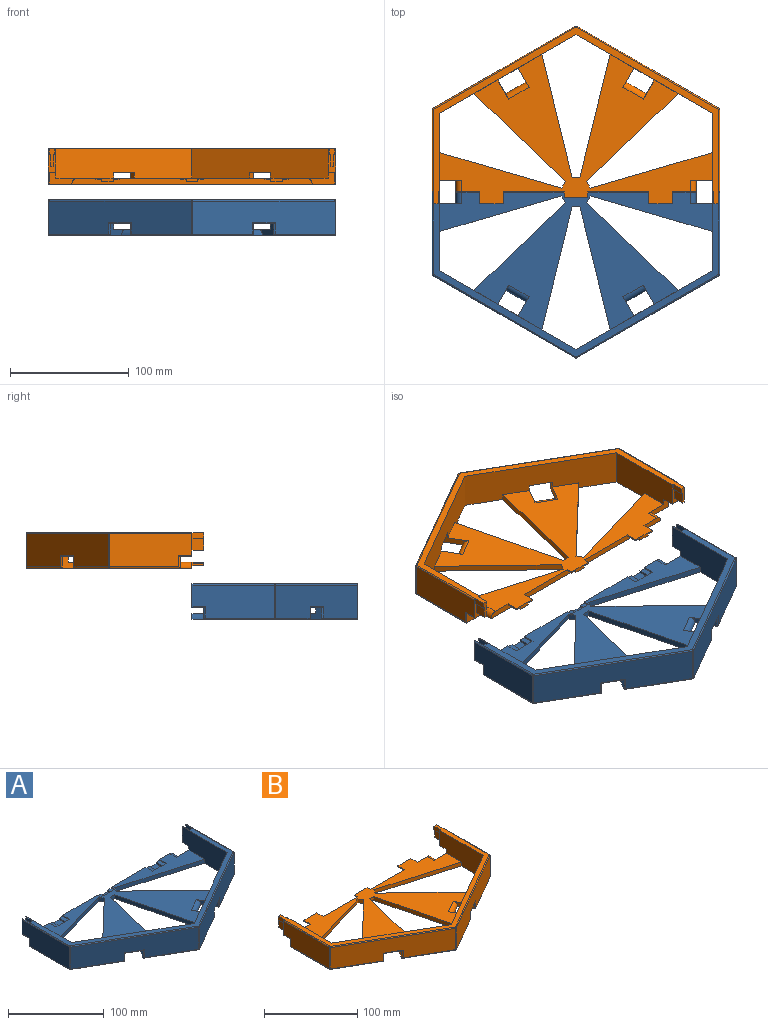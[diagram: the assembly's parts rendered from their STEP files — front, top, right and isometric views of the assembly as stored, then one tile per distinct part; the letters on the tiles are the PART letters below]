
ASSEMBLY  parts=2 mates=1
PART A: 106 faces, bbox 242.5x139.8x30 mm
  f0: plane 229.5x115.94mm, normal (0,0,1), area 9823.1mm2, adj f1,f3,f6,f8,f13,f14,f15,f16
  f1: plane 202.49x5mm, normal (0,1,0), area 870.5mm2, adj f0,f4,f49,f50,f51,f52,f53,f54
  f2: plane 240.49x138.85mm, normal (0,0,1), area 2146.7mm2, adj f3,f5,f6,f8,f9,f13,f39,f40
  f3: plane 114.75x66.25mm, normal (0.5,0.87,0), area 3543.8mm2, adj f0,f2,f4,f6,f8,f15,f20,f30
  f4: plane 240.49x138.85mm, normal (0,0,-1), area 12530mm2, adj f1,f3,f6,f8,f13,f14,f15,f16
  f5: plane 20x6.5mm, normal (0,1,0), area 82mm2, adj f2,f6,f10,f28,f41,f42,f43,f44
  f6: plane 66.25x30mm, normal (1,0,0), area 1771.9mm2, adj f0,f2,f3,f4,f5,f14,f28,f29
  f7: plane 69.42x28mm, normal (1,0,0), area 1833.8mm2, adj f9,f73,f74,f76,f82,f83
  f8: plane 114.75x66.25mm, normal (-0.5,0.87,0), area 3543.8mm2, adj f0,f2,f3,f4,f13,f18,f21,f23
  f9: plane 20x6.5mm, normal (0,1,0), area 82mm2, adj f2,f7,f13,f26,f33,f34,f35,f36
  f10: plane 69.42x28mm, normal (-1,0,0), area 1833.8mm2, adj f5,f75,f77,f79,f80,f81
  f11: plane 120.24x69.42mm, normal (-0.5,-0.87,0), area 3667.7mm2, adj f80,f89,f90,f93,f96,f97,f99,f101
  f12: plane 120.24x69.42mm, normal (0.5,-0.87,0), area 3667.7mm2, adj f83,f84,f88,f91,f92,f95,f97,f98
  f13: plane 66.25x30mm, normal (-1,0,0), area 1771.9mm2, adj f0,f2,f4,f8,f9,f17,f26,f27
  f14: plane 102.67x29.89mm, normal (0.28,-0.96,0), area 534.7mm2, adj f0,f4,f6,f16
  f15: plane 77.22x73.97mm, normal (-0.69,0.72,0), area 534.7mm2, adj f0,f3,f4,f16
  f16: plane 5.6x5mm, normal (-0.87,-0.5,0), area 32.4mm2, adj f0,f4,f14,f15
  f17: plane 102.67x29.89mm, normal (-0.28,-0.96,0), area 534.7mm2, adj f0,f4,f13,f19
  f18: plane 77.22x73.98mm, normal (0.69,0.72,0), area 534.7mm2, adj f0,f4,f8,f19
  f19: plane 5.6x5mm, normal (0.87,-0.5,0), area 32.4mm2, adj f0,f4,f17,f18
  f20: plane 103.86x25.46mm, normal (0.97,-0.24,0), area 534.7mm2, adj f0,f3,f4,f22
  f21: plane 103.86x25.46mm, normal (-0.97,-0.24,0), area 534.7mm2, adj f0,f4,f8,f22
  f22: plane 6.47x5mm, normal (0,-1,0), area 32.4mm2, adj f0,f4,f20,f21
  f23: plane 20.07x14.76mm, normal (0,0,-1), area 109.9mm2, adj f8,f24,f25,f92
  f24: plane 20.78x12mm, normal (0.87,0.5,0), area 127.8mm2, adj f0,f4,f8,f23,f95,f105
  f25: plane 20.78x12mm, normal (-0.87,-0.5,0), area 127.8mm2, adj f0,f4,f8,f23,f88,f105
  f26: plane 10x5.5mm, normal (0,0,-1), area 55mm2, adj f9,f13,f27,f73
  f27: plane 24x10mm, normal (0,1,0), area 127.8mm2, adj f0,f4,f13,f26,f74,f104
  f28: plane 10x5.5mm, normal (0,0,-1), area 55mm2, adj f5,f6,f29,f75
  f29: plane 24x10mm, normal (0,1,0), area 127.8mm2, adj f0,f4,f6,f28,f77,f103
  f30: plane 20.07x14.76mm, normal (0,0,-1), area 109.9mm2, adj f3,f31,f32,f96
  f31: plane 20.78x12mm, normal (0.87,-0.5,0), area 127.8mm2, adj f0,f3,f4,f30,f93,f102
  f32: plane 20.78x12mm, normal (-0.87,0.5,0), area 127.8mm2, adj f0,f3,f4,f30,f99,f102
  f33: plane 10x5mm, normal (-1,0,0), area 50mm2, adj f9,f34,f40,f82
  f34: plane 10x1mm, normal (0,0,1), area 10mm2, adj f9,f33,f35,f40
  f35: plane 10x10mm, normal (-1,0,0), area 100mm2, adj f9,f34,f36,f40
  f36: plane 10x2.5mm, normal (0,0,1), area 25mm2, adj f9,f35,f37,f40
  f37: plane 10x10mm, normal (1,0,0), area 100mm2, adj f9,f36,f38,f40
  f38: plane 10x1mm, normal (0,0,1), area 10mm2, adj f9,f37,f39,f40
  f39: plane 10x5mm, normal (1,0,0), area 50mm2, adj f2,f9,f38,f40
  f40: plane 15x4.5mm, normal (0,1,0), area 47.4mm2, adj f2,f33,f34,f35,f36,f37,f38,f39
  f41: plane 10x5mm, normal (-1,0,0), area 50mm2, adj f2,f5,f42,f48
  f42: plane 10x1mm, normal (0,0,1), area 10mm2, adj f5,f41,f43,f48
  f43: plane 10x10mm, normal (-1,0,0), area 100mm2, adj f5,f42,f44,f48
  f44: plane 10x2.5mm, normal (0,0,1), area 25mm2, adj f5,f43,f45,f48
  f45: plane 10x10mm, normal (1,0,0), area 100mm2, adj f5,f44,f46,f48
  f46: plane 10x1mm, normal (0,0,1), area 10mm2, adj f5,f45,f47,f48
  f47: plane 10x5mm, normal (1,0,0), area 50mm2, adj f5,f46,f48,f81
  f48: plane 15x4.5mm, normal (0,1,0), area 47.4mm2, adj f2,f41,f42,f43,f44,f45,f46,f47
  f49: plane 10x5mm, normal (0,0,1), area 50mm2, adj f1,f50,f55,f56
  f50: plane 10x1.25mm, normal (1,0,0), area 12.5mm2, adj f0,f1,f49,f56
  f51: plane 10x1.25mm, normal (-1,0,0), area 12.5mm2, adj f0,f1,f52,f56
  f52: plane 10x5mm, normal (0,0,1), area 50mm2, adj f1,f51,f53,f56
  f53: plane 10x1.88mm, normal (-1,0,0), area 18.8mm2, adj f1,f52,f54,f56
  f54: plane 10x10mm, normal (0,0,1), area 100mm2, adj f1,f53,f55,f56
  f55: plane 10x1.88mm, normal (1,0,0), area 18.8mm2, adj f1,f49,f54,f56
  f56: plane 20x3.13mm, normal (0,1,0), area 43.8mm2, adj f0,f49,f50,f51,f52,f53,f54,f55
  f57: plane 10x1.25mm, normal (-1,0,0), area 12.5mm2, adj f0,f1,f58,f64
  f58: plane 10x5mm, normal (0,0,1), area 50mm2, adj f1,f57,f59,f64
  f59: plane 10x1.88mm, normal (-1,0,0), area 18.8mm2, adj f1,f58,f60,f64
  f60: plane 10x10mm, normal (0,0,1), area 100mm2, adj f1,f59,f61,f64
  f61: plane 10x1.88mm, normal (1,0,0), area 18.8mm2, adj f1,f60,f62,f64
  f62: plane 10x5mm, normal (0,0,1), area 50mm2, adj f1,f61,f63,f64
  f63: plane 10x1.25mm, normal (1,0,0), area 12.5mm2, adj f0,f1,f62,f64
  f64: plane 20x3.13mm, normal (0,1,0), area 43.8mm2, adj f0,f57,f58,f59,f60,f61,f62,f63
  f65: plane 10x5mm, normal (0,0,1), area 50mm2, adj f1,f66,f71,f72
  f66: plane 5x1.88mm, normal (1,0,0), area 9.4mm2, adj f1,f65,f67,f72
  f67: plane 5x5mm, normal (0,0,1), area 25mm2, adj f1,f66,f68,f72
  f68: plane 5x1.25mm, normal (1,0,0), area 6.3mm2, adj f0,f1,f67,f72
  f69: plane 5x1.25mm, normal (-1,0,0), area 6.3mm2, adj f0,f1,f70,f72
  f70: plane 5x5mm, normal (0,0,1), area 25mm2, adj f1,f69,f71,f72
  f71: plane 5x1.88mm, normal (-1,0,0), area 9.4mm2, adj f1,f65,f70,f72
  f72: plane 20x3.13mm, normal (0,1,0), area 43.8mm2, adj f0,f65,f66,f67,f68,f69,f70,f71
  f73: cylinder r=1mm len=11mm, axis (0,-1,0), area 16.3mm2, adj f7,f9,f26,f74
  f74: cylinder r=1mm len=11mm, axis (0,0,-1), area 15.7mm2, adj f7,f27,f73,f76
  f75: cylinder r=1mm len=11mm, axis (0,1,0), area 16.3mm2, adj f5,f10,f28,f77
  f76: cylinder r=1mm len=59.42mm, axis (0,1,0), area 92.8mm2, adj f4,f7,f74,f78
  f77: cylinder r=1mm len=11mm, axis (0,0,1), area 15.7mm2, adj f10,f29,f75,f79
  f78: sphere r=1mm, area 1mm2, adj f76,f83,f84
  f79: cylinder r=1mm len=59.42mm, axis (0,-1,0), area 92.8mm2, adj f4,f10,f77,f85
  f80: cylinder r=1mm len=28mm, axis (0,0,-1), area 29.3mm2, adj f10,f11,f85,f86
  f81: cylinder r=1mm len=69.42mm, axis (0,1,0), area 109mm2, adj f2,f5,f10,f47,f86
  f82: cylinder r=1mm len=69.42mm, axis (0,-1,0), area 109mm2, adj f2,f7,f9,f33,f87
  f83: cylinder r=1mm len=28mm, axis (0,0,-1), area 29.3mm2, adj f7,f12,f78,f87
  f84: cylinder r=1mm len=51.96mm, axis (0.87,0.5,0), area 92.8mm2, adj f4,f12,f78,f88
  f85: sphere r=1mm, area 1mm2, adj f79,f80,f89
  f86: sphere r=1mm, area 1mm2, adj f80,f81,f90
  f87: sphere r=1mm, area 1mm2, adj f82,f83,f91
  f88: cylinder r=1mm len=11mm, axis (0,0,1), area 15.7mm2, adj f12,f25,f84,f92
  f89: cylinder r=1mm len=51.96mm, axis (0.87,-0.5,0), area 92.8mm2, adj f4,f11,f85,f93
  f90: cylinder r=1mm len=120.74mm, axis (-0.87,0.5,0), area 218.1mm2, adj f2,f11,f86,f94
  f91: cylinder r=1mm len=120.74mm, axis (-0.87,-0.5,0), area 218.1mm2, adj f2,f12,f87,f94
  f92: cylinder r=1mm len=19.55mm, axis (-0.87,-0.5,0), area 32.6mm2, adj f12,f23,f88,f95
  f93: cylinder r=1mm len=11mm, axis (0,0,-1), area 15.7mm2, adj f11,f31,f89,f96
  f94: sphere r=1mm, area 1mm2, adj f90,f91,f97
  f95: cylinder r=1mm len=11mm, axis (0,0,-1), area 15.7mm2, adj f12,f24,f92,f98
  f96: cylinder r=1mm len=19.55mm, axis (-0.87,0.5,0), area 32.6mm2, adj f11,f30,f93,f99
  f97: cylinder r=1mm len=28mm, axis (0,0,-1), area 29.3mm2, adj f11,f12,f94,f100
  f98: cylinder r=1mm len=51.96mm, axis (0.87,0.5,0), area 92.8mm2, adj f4,f12,f95,f100
  f99: cylinder r=1mm len=11mm, axis (0,0,1), area 15.7mm2, adj f11,f32,f96,f101
  f100: sphere r=1mm, area 1mm2, adj f97,f98,f101
  f101: cylinder r=1mm len=51.96mm, axis (0.87,-0.5,0), area 92.8mm2, adj f4,f11,f99,f100
  f102: cylinder r=5mm len=19.82mm, axis (0.87,-0.5,0), area 157.1mm2, adj f0,f4,f31,f32
  f103: cylinder r=5mm len=10mm, axis (0,-1,0), area 78.5mm2, adj f0,f1,f4,f29
  f104: cylinder r=5mm len=10mm, axis (0,1,0), area 78.5mm2, adj f0,f1,f4,f27
  f105: cylinder r=5mm len=19.82mm, axis (0.87,0.5,0), area 157.1mm2, adj f0,f4,f24,f25
PART B: 106 faces, bbox 242.5x149.6x30 mm
  f0: plane 202.49x5mm, normal (0,1,0), area 874.2mm2, adj f3,f5,f49,f50,f51,f52,f53,f54
  f1: plane 20x6.5mm, normal (0,1,0), area 88mm2, adj f6,f9,f12,f28,f41,f42,f43,f44
  f2: plane 20x6.5mm, normal (0,1,0), area 88mm2, adj f7,f12,f13,f26,f33,f34,f35,f36
  f3: plane 229.5x125.74mm, normal (0,0,1), area 10801.3mm2, adj f0,f4,f6,f8,f13,f14,f15,f16
  f4: plane 114.75x66.25mm, normal (0.5,0.87,0), area 3543.8mm2, adj f3,f5,f6,f8,f12,f15,f20,f30
  f5: plane 240.49x138.85mm, normal (0,0,-1), area 12530mm2, adj f0,f4,f6,f8,f13,f14,f15,f16
  f6: plane 66.25x30mm, normal (1,0,0), area 1771.9mm2, adj f1,f3,f4,f5,f12,f14,f28,f29
  f7: plane 69.42x28mm, normal (1,0,0), area 1833.8mm2, adj f2,f73,f74,f76,f82,f83
  f8: plane 114.75x66.25mm, normal (-0.5,0.87,0), area 3543.8mm2, adj f3,f4,f5,f12,f13,f18,f21,f23
  f9: plane 69.42x28mm, normal (-1,0,0), area 1833.8mm2, adj f1,f75,f77,f79,f80,f81
  f10: plane 120.24x69.42mm, normal (-0.5,-0.87,0), area 3667.7mm2, adj f80,f89,f90,f93,f96,f97,f99,f101
  f11: plane 120.24x69.42mm, normal (0.5,-0.87,0), area 3667.7mm2, adj f83,f84,f88,f91,f92,f95,f97,f98
  f12: plane 240.49x148.65mm, normal (0,0,1), area 2316.9mm2, adj f1,f2,f4,f6,f8,f13,f33,f39
  f13: plane 66.25x30mm, normal (-1,0,0), area 1771.9mm2, adj f2,f3,f5,f8,f12,f17,f26,f27
  f14: plane 102.67x29.89mm, normal (0.28,-0.96,0), area 534.7mm2, adj f3,f5,f6,f16
  f15: plane 77.22x73.97mm, normal (-0.69,0.72,0), area 534.7mm2, adj f3,f4,f5,f16
  f16: plane 5.6x5mm, normal (-0.87,-0.5,0), area 32.4mm2, adj f3,f5,f14,f15
  f17: plane 102.67x29.89mm, normal (-0.28,-0.96,0), area 534.7mm2, adj f3,f5,f13,f19
  f18: plane 77.22x73.98mm, normal (0.69,0.72,0), area 534.7mm2, adj f3,f5,f8,f19
  f19: plane 5.6x5mm, normal (0.87,-0.5,0), area 32.4mm2, adj f3,f5,f17,f18
  f20: plane 103.86x25.46mm, normal (0.97,-0.24,0), area 534.7mm2, adj f3,f4,f5,f22
  f21: plane 103.86x25.46mm, normal (-0.97,-0.24,0), area 534.7mm2, adj f3,f5,f8,f22
  f22: plane 6.47x5mm, normal (0,-1,0), area 32.4mm2, adj f3,f5,f20,f21
  f23: plane 20.07x14.76mm, normal (0,0,-1), area 109.9mm2, adj f8,f24,f25,f92
  f24: plane 20.78x12mm, normal (0.87,0.5,0), area 127.8mm2, adj f3,f5,f8,f23,f95,f105
  f25: plane 20.78x12mm, normal (-0.87,-0.5,0), area 127.8mm2, adj f3,f5,f8,f23,f88,f105
  f26: plane 10x5.5mm, normal (0,0,-1), area 55mm2, adj f2,f13,f27,f73
  f27: plane 24x10mm, normal (0,1,0), area 127.8mm2, adj f3,f5,f13,f26,f74,f104
  f28: plane 10x5.5mm, normal (0,0,-1), area 55mm2, adj f1,f6,f29,f75
  f29: plane 24x10mm, normal (0,1,0), area 127.8mm2, adj f3,f5,f6,f28,f77,f103
  f30: plane 20.07x14.76mm, normal (0,0,-1), area 109.9mm2, adj f4,f31,f32,f96
  f31: plane 20.78x12mm, normal (0.87,-0.5,0), area 127.8mm2, adj f3,f4,f5,f30,f93,f102
  f32: plane 20.78x12mm, normal (-0.87,0.5,0), area 127.8mm2, adj f3,f4,f5,f30,f99,f102
  f33: plane 9.8x5mm, normal (1,0,0), area 49mm2, adj f2,f12,f34,f40
  f34: plane 9.8x1mm, normal (0,0,-1), area 9.8mm2, adj f2,f33,f35,f40
  f35: plane 10x9.8mm, normal (1,0,0), area 98mm2, adj f2,f34,f36,f40
  f36: plane 9.8x2.1mm, normal (0,0,-1), area 20.5mm2, adj f2,f35,f37,f40
  f37: plane 10x9.8mm, normal (-1,0,0), area 98mm2, adj f2,f36,f38,f40
  f38: plane 9.8x1mm, normal (0,0,-1), area 9.8mm2, adj f2,f37,f39,f40
  f39: plane 9.8x5mm, normal (-1,0,0), area 49mm2, adj f2,f12,f38,f40
  f40: plane 15x4.1mm, normal (0,1,0), area 41.4mm2, adj f12,f33,f34,f35,f36,f37,f38,f39
  f41: plane 9.8x5mm, normal (1,0,0), area 49mm2, adj f1,f12,f42,f48
  f42: plane 9.8x1mm, normal (0,0,-1), area 9.8mm2, adj f1,f41,f43,f48
  f43: plane 10x9.8mm, normal (1,0,0), area 98mm2, adj f1,f42,f44,f48
  f44: plane 9.8x2.1mm, normal (0,0,-1), area 20.5mm2, adj f1,f43,f45,f48
  f45: plane 10x9.8mm, normal (-1,0,0), area 98mm2, adj f1,f44,f46,f48
  f46: plane 9.8x1mm, normal (0,0,-1), area 9.8mm2, adj f1,f45,f47,f48
  f47: plane 9.8x5mm, normal (-1,0,0), area 49mm2, adj f1,f12,f46,f48
  f48: plane 15x4.1mm, normal (0,1,0), area 41.4mm2, adj f12,f41,f42,f43,f44,f45,f46,f47
  f49: plane 9.8x1.25mm, normal (1,0,0), area 12.2mm2, adj f0,f3,f50,f56
  f50: plane 9.8x5mm, normal (0,0,-1), area 49mm2, adj f0,f49,f51,f56
  f51: plane 9.8x1.88mm, normal (1,0,0), area 18.4mm2, adj f0,f50,f52,f56
  f52: plane 9.8x9.6mm, normal (0,0,-1), area 94.1mm2, adj f0,f51,f53,f56
  f53: plane 9.8x1.88mm, normal (-1,0,0), area 18.4mm2, adj f0,f52,f54,f56
  f54: plane 9.8x5mm, normal (0,0,-1), area 49mm2, adj f0,f53,f55,f56
  f55: plane 9.8x1.25mm, normal (-1,0,0), area 12.2mm2, adj f0,f3,f54,f56
  f56: plane 19.6x3.13mm, normal (0,1,0), area 42.5mm2, adj f3,f49,f50,f51,f52,f53,f54,f55
  f57: plane 9.8x5mm, normal (0,0,-1), area 49mm2, adj f0,f58,f63,f64
  f58: plane 9.8x1.25mm, normal (-1,0,0), area 12.2mm2, adj f0,f3,f57,f64
  f59: plane 9.8x1.25mm, normal (1,0,0), area 12.2mm2, adj f0,f3,f60,f64
  f60: plane 9.8x5mm, normal (0,0,-1), area 49mm2, adj f0,f59,f61,f64
  f61: plane 9.8x1.88mm, normal (1,0,0), area 18.4mm2, adj f0,f60,f62,f64
  f62: plane 9.8x9.6mm, normal (0,0,-1), area 94.1mm2, adj f0,f61,f63,f64
  f63: plane 9.8x1.88mm, normal (-1,0,0), area 18.4mm2, adj f0,f57,f62,f64
  f64: plane 19.6x3.13mm, normal (0,1,0), area 42.5mm2, adj f3,f57,f58,f59,f60,f61,f62,f63
  f65: plane 9.6x4.8mm, normal (0,0,-1), area 46.1mm2, adj f0,f66,f71,f72
  f66: plane 4.8x1.88mm, normal (-1,0,0), area 9mm2, adj f0,f65,f67,f72
  f67: plane 5x4.8mm, normal (0,0,-1), area 24mm2, adj f0,f66,f68,f72
  f68: plane 4.8x1.25mm, normal (-1,0,0), area 6mm2, adj f0,f3,f67,f72
  f69: plane 4.8x1.25mm, normal (1,0,0), area 6mm2, adj f0,f3,f70,f72
  f70: plane 5x4.8mm, normal (0,0,-1), area 24mm2, adj f0,f69,f71,f72
  f71: plane 4.8x1.88mm, normal (1,0,0), area 9mm2, adj f0,f65,f70,f72
  f72: plane 19.6x3.13mm, normal (0,1,0), area 42.5mm2, adj f3,f65,f66,f67,f68,f69,f70,f71
  f73: cylinder r=1mm len=11mm, axis (0,-1,0), area 16.3mm2, adj f2,f7,f26,f74
  f74: cylinder r=1mm len=11mm, axis (0,0,-1), area 15.7mm2, adj f7,f27,f73,f76
  f75: cylinder r=1mm len=11mm, axis (0,1,0), area 16.3mm2, adj f1,f9,f28,f77
  f76: cylinder r=1mm len=59.42mm, axis (0,1,0), area 92.8mm2, adj f5,f7,f74,f78
  f77: cylinder r=1mm len=11mm, axis (0,0,1), area 15.7mm2, adj f9,f29,f75,f79
  f78: sphere r=1mm, area 1mm2, adj f76,f83,f84
  f79: cylinder r=1mm len=59.42mm, axis (0,-1,0), area 92.8mm2, adj f5,f9,f77,f85
  f80: cylinder r=1mm len=28mm, axis (0,0,-1), area 29.3mm2, adj f9,f10,f85,f86
  f81: cylinder r=1mm len=69.42mm, axis (0,1,0), area 109mm2, adj f1,f9,f12,f86
  f82: cylinder r=1mm len=69.42mm, axis (0,-1,0), area 109mm2, adj f2,f7,f12,f87
  f83: cylinder r=1mm len=28mm, axis (0,0,-1), area 29.3mm2, adj f7,f11,f78,f87
  f84: cylinder r=1mm len=51.96mm, axis (0.87,0.5,0), area 92.8mm2, adj f5,f11,f78,f88
  f85: sphere r=1mm, area 1mm2, adj f79,f80,f89
  f86: sphere r=1mm, area 1mm2, adj f80,f81,f90
  f87: sphere r=1mm, area 1mm2, adj f82,f83,f91
  f88: cylinder r=1mm len=11mm, axis (0,0,1), area 15.7mm2, adj f11,f25,f84,f92
  f89: cylinder r=1mm len=51.96mm, axis (0.87,-0.5,0), area 92.8mm2, adj f5,f10,f85,f93
  f90: cylinder r=1mm len=120.74mm, axis (-0.87,0.5,0), area 218.1mm2, adj f10,f12,f86,f94
  f91: cylinder r=1mm len=120.74mm, axis (-0.87,-0.5,0), area 218.1mm2, adj f11,f12,f87,f94
  f92: cylinder r=1mm len=19.55mm, axis (-0.87,-0.5,0), area 32.6mm2, adj f11,f23,f88,f95
  f93: cylinder r=1mm len=11mm, axis (0,0,-1), area 15.7mm2, adj f10,f31,f89,f96
  f94: sphere r=1mm, area 1mm2, adj f90,f91,f97
  f95: cylinder r=1mm len=11mm, axis (0,0,-1), area 15.7mm2, adj f11,f24,f92,f98
  f96: cylinder r=1mm len=19.55mm, axis (-0.87,0.5,0), area 32.6mm2, adj f10,f30,f93,f99
  f97: cylinder r=1mm len=28mm, axis (0,0,-1), area 29.3mm2, adj f10,f11,f94,f100
  f98: cylinder r=1mm len=51.96mm, axis (0.87,0.5,0), area 92.8mm2, adj f5,f11,f95,f100
  f99: cylinder r=1mm len=11mm, axis (0,0,1), area 15.7mm2, adj f10,f32,f96,f101
  f100: sphere r=1mm, area 1mm2, adj f97,f98,f101
  f101: cylinder r=1mm len=51.96mm, axis (0.87,-0.5,0), area 92.8mm2, adj f5,f10,f99,f100
  f102: cylinder r=5mm len=19.82mm, axis (0.87,-0.5,0), area 157.1mm2, adj f3,f5,f31,f32
  f103: cylinder r=5mm len=10mm, axis (0,-1,0), area 78.5mm2, adj f0,f3,f5,f29
  f104: cylinder r=5mm len=10mm, axis (0,1,0), area 78.5mm2, adj f0,f3,f5,f27
  f105: cylinder r=5mm len=19.82mm, axis (0.87,0.5,0), area 157.1mm2, adj f3,f5,f24,f25
PLACE A at identity
PLACE B rot(axis=(0,0,1),180deg) t=(0,0,43.26)mm
MATE slider B.f5 <-> A.f4  axis (0,0,-1) through (0,0,43.26)mm
